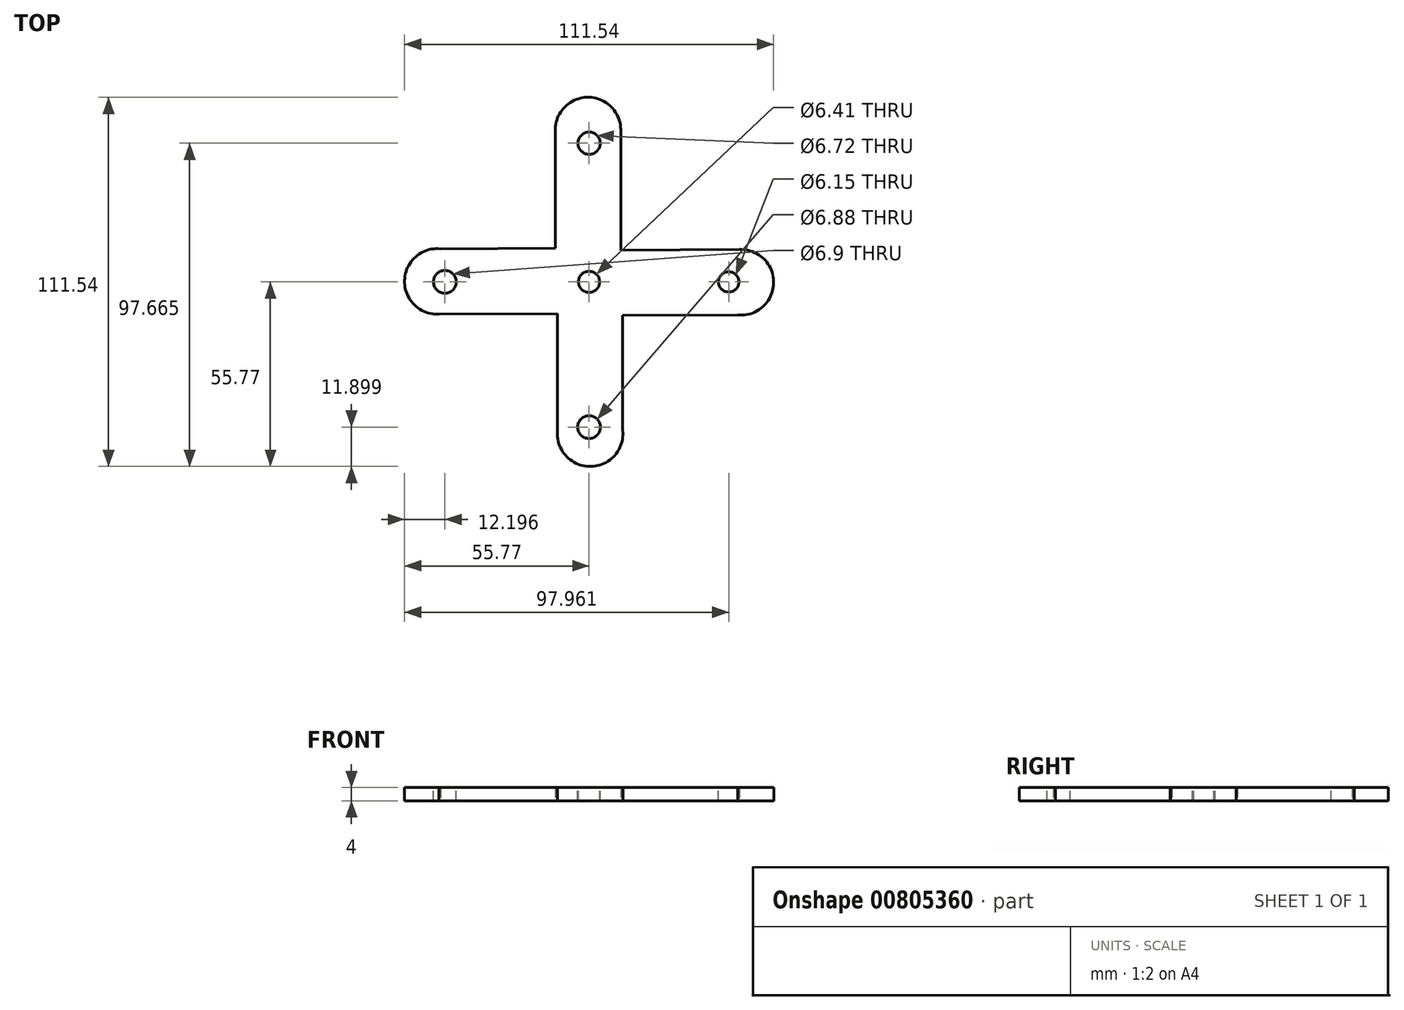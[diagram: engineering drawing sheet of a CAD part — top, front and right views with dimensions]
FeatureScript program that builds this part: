
annotation { "Feature Type Name" : "Feature", "Feature Type Description" : "" }
export const myFeature = defineFeature(function(context is Context, id is Id, definition is map)
    precondition{}
    {
        {
            var Q0;
            Q0=qCreatedBy(makeId("Top.planeOp"),FACE);
            var sketch = newSketch(context, id + "F0", { "sketchPlane" : qUnion([Q0])});
            skLineSegment(sketch, "E0", {"start": v(0, 0) * mm, "end": v(0, 74.7) * mm});
            skLineSegment(sketch, "E1", {"start": v(0, 0) * mm, "end": v(0, -74.7) * mm});
            skLineSegment(sketch, "E2", {"start": v(0, 0) * mm, "end": v(-74.8, 0) * mm});
            skLineSegment(sketch, "E3", {"start": v(0, 0) * mm, "end": v(75, 0) * mm});
            skLineSegment(sketch, "E4", {"start": v(0, 0) * mm, "end": v(75, -74.7) * mm});
            skLineSegment(sketch, "E5", {"start": v(0, 0) * mm, "end": v(-74.4, -74.7) * mm});
            skLineSegment(sketch, "E6", {"start": v(0, 0) * mm, "end": v(75, 75.3) * mm});
            skLineSegment(sketch, "E7", {"start": v(0, 0) * mm, "end": v(-75.6, 75.3) * mm});
            skArc(sketch, "E8", {"start": v(9.58, 45.45) * mm, "mid": v(-0.61, 55.77) * mm, "end": v(-10.18, 44.86) * mm});
            skLineSegment(sketch, "E9", {"start": v(-10.18, 44.86) * mm, "end": v(-10.18, 10.14) * mm});
            skLineSegment(sketch, "E10", {"start": v(9.58, 45.45) * mm, "end": v(9.58, 9.62) * mm});
            skLineSegment(sketch, "E11.MirrorCS", {"start": v(45.41, 9.76) * mm, "end": v(9.58, 9.62) * mm});
            skArc(sketch, "E12.MirrorCS", {"start": v(45.41, 9.76) * mm, "mid": v(55.77, -0.4) * mm, "end": v(44.9, -10) * mm});
            skLineSegment(sketch, "E13.MirrorCS", {"start": v(44.9, -10) * mm, "end": v(10.18, -10.14) * mm});
            skLineSegment(sketch, "E14.MirrorCS", {"start": v(10.18, -44.86) * mm, "end": v(10.18, -10.14) * mm});
            skArc(sketch, "E15.MirrorCS", {"start": v(-9.58, -45.45) * mm, "mid": v(0.61, -55.77) * mm, "end": v(10.18, -44.86) * mm});
            skLineSegment(sketch, "E16.MirrorCS", {"start": v(-9.58, -45.45) * mm, "end": v(-9.58, -9.62) * mm});
            skLineSegment(sketch, "E17.MirrorCS", {"start": v(-45.41, -9.76) * mm, "end": v(-9.58, -9.62) * mm});
            skArc(sketch, "E18.MirrorCS", {"start": v(-45.41, -9.76) * mm, "mid": v(-55.77, 0.4) * mm, "end": v(-44.9, 10) * mm});
            skLineSegment(sketch, "E19.MirrorCS", {"start": v(-44.9, 10) * mm, "end": v(-10.18, 10.14) * mm});
            skSolve(sketch);
        }
        {
            var Q0;
            Q0 = qSketchRegion(id + "F0", true);
            extrude(context, id + "F1", {"entities" : qUnion([Q0]), "depth" : 4 * mm, "offsetDistance" : 25 * mm});
        }
        {
            var Q0;
            Q0=makeQuery(id+"F1.opExtrude","CAP_FACE",FACE,{"disambiguationData":[OSD([sQuery(id+"F0.wireOp",EDGE,"E8"),sQuery(id+"F0.wireOp",EDGE,"E9"),sQuery(id+"F0.wireOp",EDGE,"E10"),sQuery(id+"F0.wireOp",EDGE,"E11.MirrorCS"),sQuery(id+"F0.wireOp",EDGE,"E12.MirrorCS"),sQuery(id+"F0.wireOp",EDGE,"E13.MirrorCS"),sQuery(id+"F0.wireOp",EDGE,"E14.MirrorCS"),sQuery(id+"F0.wireOp",EDGE,"E15.MirrorCS"),sQuery(id+"F0.wireOp",EDGE,"E16.MirrorCS"),sQuery(id+"F0.wireOp",EDGE,"E17.MirrorCS"),sQuery(id+"F0.wireOp",EDGE,"E18.MirrorCS"),sQuery(id+"F0.wireOp",EDGE,"E19.MirrorCS")])],"isStart":false});
            var sketch = newSketch(context, id + "F2", { "sketchPlane" : qUnion([Q0])});
            skCircle(sketch, "E20", {"center": v(0, 0) * mm, "radius": 3.2 * mm});
            skCircle(sketch, "E21", {"center": v(-43.57, 0) * mm, "radius": 3.45 * mm});
            skCircle(sketch, "E22", {"center": v(0, -43.87) * mm, "radius": 3.44 * mm});
            skCircle(sketch, "E23", {"center": v(42.2, 0) * mm, "radius": 3.07 * mm});
            skCircle(sketch, "E24", {"center": v(0, 41.9) * mm, "radius": 3.36 * mm});
            skSolve(sketch);
        }
        {
            var Q0;
            Q0 = qSketchRegion(id + "F2", true);
            extrude(context, id + "F3", {"entities" : qUnion([Q0]), "operationType" : NewBodyOperationType.REMOVE, "oppositeDirection" : true, "depth" : 114.2 * mm, "offsetDistance" : 25 * mm});
        }
    });
